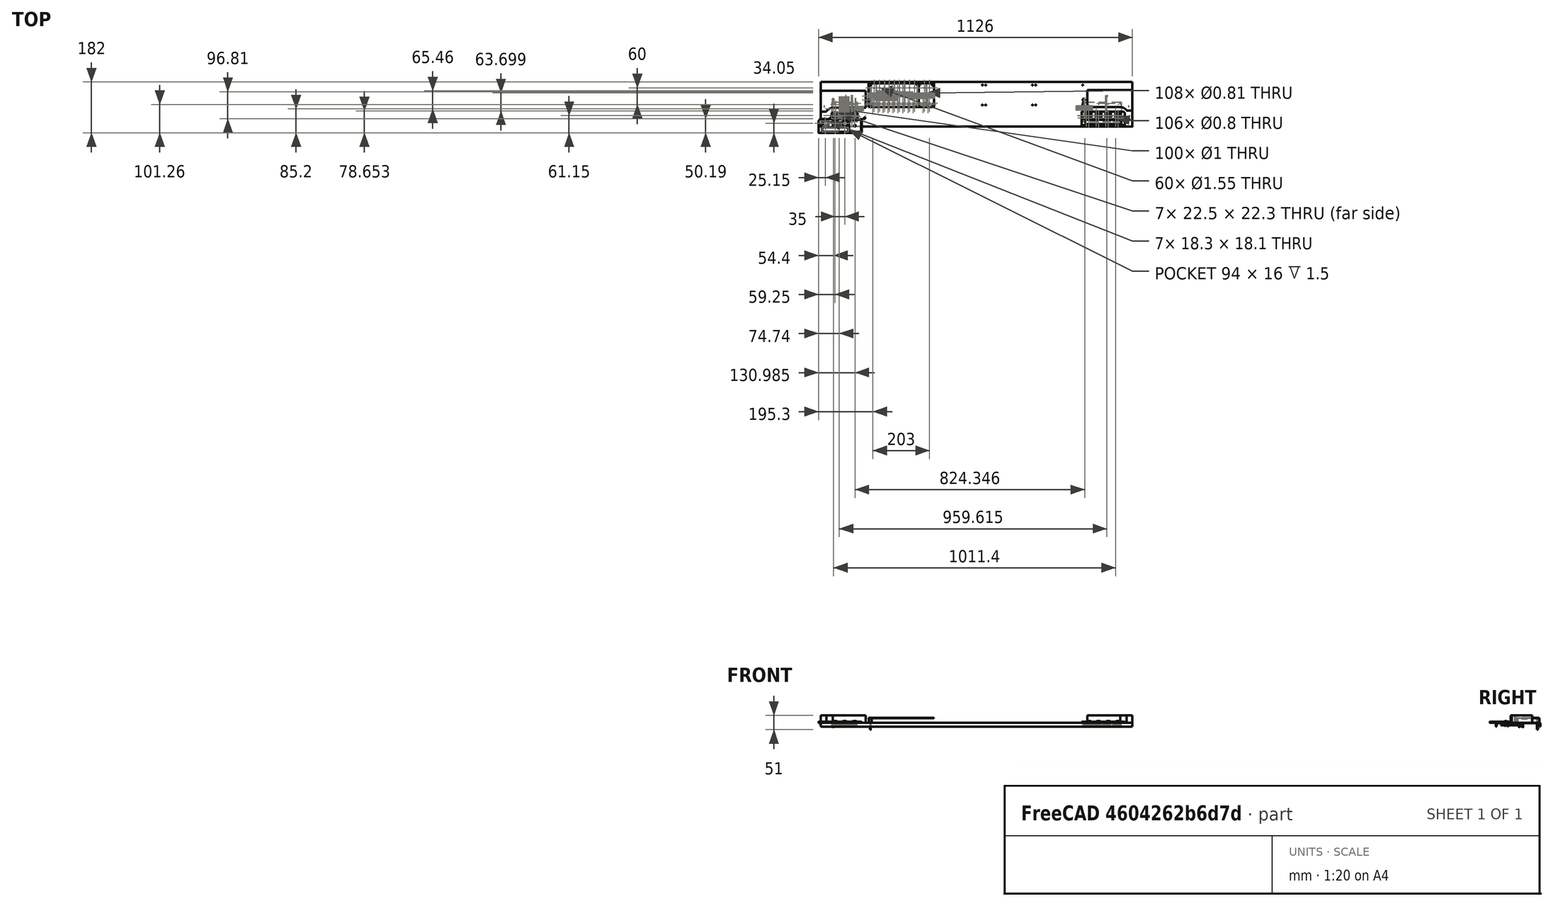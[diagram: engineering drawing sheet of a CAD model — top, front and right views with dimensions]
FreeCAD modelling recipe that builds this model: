
FCSTD DOCUMENT  (FreeCAD 0.20R29603 (Git))
Label: panneau-commandes-assy
License: Public Domain
LicenseURL: http://en.wikipedia.org/wiki/Public_domain
objects: App::FeaturePython×46, Part::FeaturePython×19, PartDesign::CoordinateSystem×2
note: 21 computed .brp shape members not serialized (recipe doc carries the construction recipe); baked Part::Feature solids carry a one-line shape summary decoded from their .brp

FEATURE [Part::FeaturePython] b_PanneauCommandeSupportTirettes_001_  label="PanneauCommandeSupportTirettes_001"  # a2plus imported part (geometry in sourceFile) (typed FeaturePython)
  a2p_Version = 0.4.60k
  fixedPosition = true
  muxInfo = <blob: 10594 chars omitted>
  objectType = a2pPart
  sourceFile = ./../Alu/PanneauCommandeSupportTirettes.FCStd
  subassemblyImport = false
  timeLastImport = 1.68744e+09
  updateColors = true
FEATURE [Part::FeaturePython] b_EnjoliveurBoutonsGaucheAvecFixation_001_  label="EnjoliveurBoutonsGaucheAvecFixation_001"  # a2plus imported part (geometry in sourceFile) (typed FeaturePython)
  Placement = pos=(-8,-25,-1.58671e-06) rot=(0,0,1;0rad)
  a2p_Version = 0.4.60k
  fixedPosition = false
  muxInfo = <blob: 7269 chars omitted>
  objectType = a2pPart
  sourceFile = ./../Accessoires/EnjoliveurBoutonsGaucheAvecFixation.FCStd
  subassemblyImport = false
  timeLastImport = 1.68148e+09
  updateColors = true
FEATURE [Part::FeaturePython] b_BlocLateralPanneauControle_001_  label="BlocLateralPanneauControle_001"  # a2plus imported part (geometry in sourceFile) (typed FeaturePython)
  Placement = pos=(0,51,0) rot=(0,0,1;0rad)
  a2p_Version = 0.4.60k
  fixedPosition = false
  muxInfo = [VERTEXES] | V;Pad;1; | V;Pad;2; | V;Pad;3; | V;Pad;4; | V;Pad;5; | V;Pad;6; | V;Pad;7; | V;Pad;8; | V;Pad;9; | V;Pad;10; | V;Pad;11; | V;Pad;12; | [EDGES] | E;Pad;1; | E;Pad;2; | E;Pad;3; | E;Pad;4; | E;Pad;5; | E;Pad;6; | E;Pad;7; | E;Pad;8; | E;Pad;9; | E;Pad;10; | E;Pad;11; | E;Pad;12; | E;Pad;13; | E;Pad;14; | E;Pad;15; | E;Pad;16; | E;Pad;17; | E;Pad;18; | [FACES] | F;Pad;1; | F;Pad;2; | F;Pad;3; | F;Pad;4; | F;Pad;5; | F;Pad;6; | F;Pad;7; | F;Pad;8;
  objectType = a2pPart
  sourceFile = ./../Menuiserie/BlocLateralPanneauControle.fcstd
  subassemblyImport = false
  timeLastImport = 1.68025e+09
  updateColors = true
FEATURE [Part::FeaturePython] b_BlocLateralPanneauControle_001_001  label="BlocLateralPanneauControle_002"  # a2plus imported part (geometry in sourceFile) (typed FeaturePython)
  Placement = pos=(1118,54.2049,26) rot=(0,1,0;3.14159rad)
  a2p_Version = 0.4.60k
  fixedPosition = false
  muxInfo = [VERTEXES] | V;Pad;1; | V;Pad;2; | V;Pad;3; | V;Pad;4; | V;Pad;5; | V;Pad;6; | V;Pad;7; | V;Pad;8; | V;Pad;9; | V;Pad;10; | V;Pad;11; | V;Pad;12; | [EDGES] | E;Pad;1; | E;Pad;2; | E;Pad;3; | E;Pad;4; | E;Pad;5; | E;Pad;6; | E;Pad;7; | E;Pad;8; | E;Pad;9; | E;Pad;10; | E;Pad;11; | E;Pad;12; | E;Pad;13; | E;Pad;14; | E;Pad;15; | E;Pad;16; | E;Pad;17; | E;Pad;18; | [FACES] | F;Pad;1; | F;Pad;2; | F;Pad;3; | F;Pad;4; | F;Pad;5; | F;Pad;6; | F;Pad;7; | F;Pad;8;
  objectType = a2pPart
  sourceFile = ./../Menuiserie/BlocLateralPanneauControle.fcstd
  subassemblyImport = false
  timeLastImport = 1.68148e+09
  updateColors = true
FEATURE [Part::FeaturePython] b_EnjoliveurBoutonsDroiteAvecFixation_001_  label="EnjoliveurBoutonsDroiteAvecFixation_001"  # a2plus imported part (geometry in sourceFile) (typed FeaturePython)
  Placement = pos=(936.6,2.1,2.92325e-06) rot=(0,0,1;0rad)
  a2p_Version = 0.4.60k
  fixedPosition = false
  muxInfo = <blob: 8591 chars omitted>
  objectType = a2pPart
  sourceFile = ./../Accessoires/EnjoliveurBoutonsDroiteAvecFixation.FCStd
  subassemblyImport = false
  timeLastImport = 1.68148e+09
  updateColors = true
FEATURE [Part::FeaturePython] b_percussions_expr_pedal_001_  label="percussions_expr_pedal_001"  # a2plus imported part (geometry in sourceFile) (typed FeaturePython)
  Placement = pos=(939.7,14.3,-9.58) rot=(0,0,1;0rad)
  a2p_Version = 0.4.60k
  fixedPosition = false
  muxInfo = <blob: 161799 chars omitted>
  objectType = a2pPart
  sourceFile = ./percussions_expr_pedal.FCStd
  subassemblyImport = false
  timeLastImport = 1.68025e+09
  updateColors = true
FEATURE [Part::FeaturePython] b_vibrato_chorus_leslie_001_  label="vibrato_chorus_leslie_001"  # a2plus imported part (geometry in sourceFile) (typed FeaturePython)
  Placement = pos=(41.1,85.2,-9.58) rot=(0,0,1;0rad)
  a2p_Version = 0.4.60k
  fixedPosition = false
  muxInfo = <blob: 126907 chars omitted>
  objectType = a2pPart
  sourceFile = ./vibrato_chorus_leslie.FCStd
  subassemblyImport = false
  timeLastImport = 1.68025e+09
  updateColors = true
FEATURE [App::FeaturePython] axisCoincident_002  label="axisCoincident_002__PanneauCommandeSupportTirettes_001"  # a2plus constraint (typed FeaturePython)
  Object1 = b_percussions_expr_pedal_001_
  Object2 = b_PanneauCommandeSupportTirettes_001_
  ParentTreeObject = -> b_percussions_expr_pedal_001_
  SubElement1 = Edge834
  SubElement2 = Edge197
  Suppressed = false
  Type = axial
  directionConstraint = 0
  lockRotation = false
FEATURE [App::FeaturePython] axisCoincident_002_mirror  label="axisCoincident_002__percussions_expr_pedal_001"  # a2plus constraint (typed FeaturePython)
  Object1 = b_percussions_expr_pedal_001_
  Object2 = b_PanneauCommandeSupportTirettes_001_
  ParentTreeObject = -> b_PanneauCommandeSupportTirettes_001_
  SubElement1 = Edge834
  SubElement2 = Edge197
  Suppressed = false
  Type = axial
  directionConstraint = 0
  lockRotation = false
FEATURE [App::FeaturePython] planeCoincident_002  label="planeCoincident_002__percussions_expr_pedal_001"  # a2plus constraint (typed FeaturePython)
  Object1 = b_PanneauCommandeSupportTirettes_001_
  Object2 = b_percussions_expr_pedal_001_
  ParentTreeObject = -> b_PanneauCommandeSupportTirettes_001_
  SubElement1 = Face12
  SubElement2 = Face265
  Suppressed = false
  Type = plane
  directionConstraint = 1
  offset = 6
FEATURE [App::FeaturePython] planeCoincident_002_mirror  label="planeCoincident_002__PanneauCommandeSupportTirettes_001"  # a2plus constraint (typed FeaturePython)
  Object1 = b_PanneauCommandeSupportTirettes_001_
  Object2 = b_percussions_expr_pedal_001_
  ParentTreeObject = -> b_percussions_expr_pedal_001_
  SubElement1 = Face12
  SubElement2 = Face265
  Suppressed = false
  Type = plane
  directionConstraint = 1
  offset = 6
FEATURE [Part::FeaturePython] b_entretoise_cartes_vc_perc_001_  label="entretoise-cartes-vc-perc_001"  # a2plus imported part (geometry in sourceFile) (typed FeaturePython)
  Placement = pos=(44.8,81.5,-8) rot=(0,0,1;0rad)
  a2p_Version = 0.4.60k
  fixedPosition = false
  muxInfo = [VERTEXES] | V;Pad;1;4; | V;Pad;2;4; | V;Pad;3;4; | V;Pad;4;4; | [EDGES] | E;Pad;1;6; | E;Pad;2;6; | E;Pad;3;6; | E;Pad;4;6; | E;Pad;5;6; | E;Pad;6;6; | [FACES] | F;Pad;1;4; | F;Pad;2;4; | F;Pad;3;4; | F;Pad;4;4;
  objectType = a2pPart
  sourceFile = ./../Accessoires/entretoise-cartes-vc-perc.FCStd
  subassemblyImport = false
  timeLastImport = 1.68025e+09
  updateColors = true
FEATURE [App::FeaturePython] planeCoincident_003  label="planeCoincident_003__PanneauCommandeSupportTirettes_001"  # a2plus constraint (typed FeaturePython)
  Object1 = b_entretoise_cartes_vc_perc_001_
  Object2 = b_PanneauCommandeSupportTirettes_001_
  ParentTreeObject = -> b_entretoise_cartes_vc_perc_001_
  SubElement1 = Face4
  SubElement2 = Face12
  Suppressed = false
  Type = plane
  directionConstraint = 0
  offset = 0
FEATURE [App::FeaturePython] planeCoincident_003_mirror  label="planeCoincident_003__entretoise-cartes-vc-perc_001"  # a2plus constraint (typed FeaturePython)
  Object1 = b_entretoise_cartes_vc_perc_001_
  Object2 = b_PanneauCommandeSupportTirettes_001_
  ParentTreeObject = -> b_PanneauCommandeSupportTirettes_001_
  SubElement1 = Face4
  SubElement2 = Face12
  Suppressed = false
  Type = plane
  directionConstraint = 0
  offset = 0
FEATURE [App::FeaturePython] axisCoincident_003  label="axisCoincident_003__PanneauCommandeSupportTirettes_001"  # a2plus constraint (typed FeaturePython)
  Object1 = b_entretoise_cartes_vc_perc_001_
  Object2 = b_PanneauCommandeSupportTirettes_001_
  ParentTreeObject = -> b_entretoise_cartes_vc_perc_001_
  SubElement1 = Edge3
  SubElement2 = Edge77
  Suppressed = false
  Type = axial
  directionConstraint = 0
  lockRotation = false
FEATURE [App::FeaturePython] axisCoincident_003_mirror  label="axisCoincident_003__entretoise-cartes-vc-perc_001"  # a2plus constraint (typed FeaturePython)
  Object1 = b_entretoise_cartes_vc_perc_001_
  Object2 = b_PanneauCommandeSupportTirettes_001_
  ParentTreeObject = -> b_PanneauCommandeSupportTirettes_001_
  SubElement1 = Edge3
  SubElement2 = Edge77
  Suppressed = false
  Type = axial
  directionConstraint = 0
  lockRotation = false
FEATURE [Part::FeaturePython] Screw  label="M3x16-Screw"  # Fasteners workbench fastener (typed FeaturePython)
  Placement = pos=(44.8,81.5,0) rot=(0,0,1;0rad)
  diameter = 4
  invert = false
  leftHanded = false
  length = 6
  lengthCustom = 16
  matchOuter = false
  offset = 0
  thread = true
  type = 47
FEATURE [App::FeaturePython] planeCoincident_004  label="planeCoincident_004__PanneauCommandeSupportTirettes_001"  # a2plus constraint (typed FeaturePython)
  Object1 = b_vibrato_chorus_leslie_001_
  Object2 = b_PanneauCommandeSupportTirettes_001_
  ParentTreeObject = -> b_vibrato_chorus_leslie_001_
  SubElement1 = Face785
  SubElement2 = Face12
  Suppressed = false
  Type = plane
  directionConstraint = 1
  offset = 6
FEATURE [App::FeaturePython] planeCoincident_004_mirror  label="planeCoincident_004__vibrato_chorus_leslie_001"  # a2plus constraint (typed FeaturePython)
  Object1 = b_vibrato_chorus_leslie_001_
  Object2 = b_PanneauCommandeSupportTirettes_001_
  ParentTreeObject = -> b_PanneauCommandeSupportTirettes_001_
  SubElement1 = Face785
  SubElement2 = Face12
  Suppressed = false
  Type = plane
  directionConstraint = 1
  offset = 6
FEATURE [App::FeaturePython] planeCoincident_005_mirror  label="planeCoincident_005__M6-Washer"  # a2plus constraint (typed FeaturePython)
  Object1 = Washer
  Object2 = b_vibrato_chorus_leslie_001_
  ParentTreeObject = -> b_vibrato_chorus_leslie_001_
  SubElement1 = Face1
  SubElement2 = Face784
  Suppressed = false
  Type = plane
  directionConstraint = 1
  offset = 0
FEATURE [App::FeaturePython] axisCoincident_004_mirror  label="axisCoincident_004__M4-Washer"  # a2plus constraint (typed FeaturePython)
  Object1 = Washer
  Object2 = b_vibrato_chorus_leslie_001_
  ParentTreeObject = -> b_vibrato_chorus_leslie_001_
  SubElement1 = Edge5
  SubElement2 = Edge2334
  Suppressed = false
  Type = axial
  directionConstraint = 0
  lockRotation = false
FEATURE [Part::FeaturePython] Washer  label="#5-Washer"  # Fasteners workbench fastener (typed FeaturePython)
  Placement = pos=(44.8,81.5,-10.3928) rot=(0,0,1;0rad)
  diameter = 6
  invert = false
  matchOuter = false
  offset = 0
  type = 0
FEATURE [App::FeaturePython] planeCoincident_005  label="planeCoincident_005__vibrato_chorus_leslie_001"  # a2plus constraint (typed FeaturePython)
  Object1 = Washer
  Object2 = b_vibrato_chorus_leslie_001_
  ParentTreeObject = -> Washer
  SubElement1 = Face1
  SubElement2 = Face784
  Suppressed = false
  Type = plane
  directionConstraint = 1
  offset = 0
FEATURE [App::FeaturePython] axisCoincident_004  label="axisCoincident_004__vibrato_chorus_leslie_001"  # a2plus constraint (typed FeaturePython)
  Object1 = Washer
  Object2 = b_vibrato_chorus_leslie_001_
  ParentTreeObject = -> Washer
  SubElement1 = Edge5
  SubElement2 = Edge2334
  Suppressed = false
  Type = axial
  directionConstraint = 0
  lockRotation = false
FEATURE [App::FeaturePython] planeCoincident_006  label="planeCoincident_006__vibrato_chorus_leslie_001"  # a2plus constraint (typed FeaturePython)
  Object1 = Washer
  Object2 = b_vibrato_chorus_leslie_001_
  ParentTreeObject = -> Washer
  SubElement1 = Face1
  SubElement2 = Face784
  Suppressed = false
  Type = plane
  directionConstraint = 1
  offset = 0
FEATURE [App::FeaturePython] planeCoincident_006_mirror  label="planeCoincident_006__#5-Washer"  # a2plus constraint (typed FeaturePython)
  Object1 = Washer
  Object2 = b_vibrato_chorus_leslie_001_
  ParentTreeObject = -> b_vibrato_chorus_leslie_001_
  SubElement1 = Face1
  SubElement2 = Face784
  Suppressed = false
  Type = plane
  directionConstraint = 1
  offset = 0
FEATURE [Part::FeaturePython] Nut  label="M3-Nut"  # Fasteners workbench fastener (typed FeaturePython)
  Placement = pos=(44.8,81.5,-12.7928) rot=(0,0,1;0rad)
  diameter = 4
  invert = false
  leftHanded = false
  matchOuter = false
  offset = 0
  thread = false
  type = 22
FEATURE [App::FeaturePython] planeCoincident_007  label="planeCoincident_007__#5-Washer"  # a2plus constraint (typed FeaturePython)
  Object1 = Nut
  Object2 = Washer
  ParentTreeObject = -> Nut
  SubElement1 = Face3
  SubElement2 = Face3
  Suppressed = false
  Type = plane
  directionConstraint = 0
  offset = 0
FEATURE [App::FeaturePython] planeCoincident_007_mirror  label="planeCoincident_007__M6-Nut"  # a2plus constraint (typed FeaturePython)
  Object1 = Nut
  Object2 = Washer
  ParentTreeObject = -> Washer
  SubElement1 = Face3
  SubElement2 = Face3
  Suppressed = false
  Type = plane
  directionConstraint = 0
  offset = 0
FEATURE [App::FeaturePython] axisCoincident_005  label="axisCoincident_005__#5-Washer"  # a2plus constraint (typed FeaturePython)
  Object1 = Nut
  Object2 = Washer
  ParentTreeObject = -> Nut
  SubElement1 = Edge4
  SubElement2 = Edge3
  Suppressed = false
  Type = axial
  directionConstraint = 0
  lockRotation = false
FEATURE [App::FeaturePython] axisCoincident_005_mirror  label="axisCoincident_005__M6-Nut"  # a2plus constraint (typed FeaturePython)
  Object1 = Nut
  Object2 = Washer
  ParentTreeObject = -> Washer
  SubElement1 = Edge4
  SubElement2 = Edge3
  Suppressed = false
  Type = axial
  directionConstraint = 0
  lockRotation = false
FEATURE [App::FeaturePython] planeCoincident_008  label="planeCoincident_008__#5-Washer"  # a2plus constraint (typed FeaturePython)
  Object1 = Nut
  Object2 = Washer
  ParentTreeObject = -> Nut
  SubElement1 = Face3
  SubElement2 = Face3
  Suppressed = false
  Type = plane
  directionConstraint = 0
  offset = 0
FEATURE [App::FeaturePython] planeCoincident_008_mirror  label="planeCoincident_008__M3-Nut"  # a2plus constraint (typed FeaturePython)
  Object1 = Nut
  Object2 = Washer
  ParentTreeObject = -> Washer
  SubElement1 = Face3
  SubElement2 = Face3
  Suppressed = false
  Type = plane
  directionConstraint = 0
  offset = 0
FEATURE [Part::FeaturePython] Screw001  label="M2x6-Screw"  # Fasteners workbench fastener (typed FeaturePython)
  Placement = pos=(-1.35631e-08,-8.06109e-09,0.999998) rot=(0,0,1;0rad)
  diameter = 2
  invert = false
  leftHanded = false
  length = 10
  lengthCustom = 6
  matchOuter = false
  offset = 0
  thread = true
  type = 46
FEATURE [App::FeaturePython] planeCoincident_011  label="planeCoincident_011__M6-Washer"  # a2plus constraint (typed FeaturePython)
  Object1 = Screw002
  Object2 = Washer001
  SubElement1 = Face11
  SubElement2 = Face1
  Suppressed = false
  Type = plane
  directionConstraint = 0
  offset = 0
FEATURE [App::FeaturePython] planeCoincident_011_mirror  label="planeCoincident_011__M6x12-Screw"  # a2plus constraint (typed FeaturePython)
  Object1 = Screw002
  Object2 = Washer001
  SubElement1 = Face11
  SubElement2 = Face1
  Suppressed = false
  Type = plane
  directionConstraint = 0
  offset = 0
FEATURE [App::FeaturePython] planeCoincident_012  label="planeCoincident_012__PanneauCommandeSupportTirettes_001"  # a2plus constraint (typed FeaturePython)
  Object1 = Washer001
  Object2 = b_PanneauCommandeSupportTirettes_001_
  SubElement1 = Face3
  SubElement2 = Face11
  Suppressed = false
  Type = plane
  directionConstraint = 0
  offset = 0
FEATURE [App::FeaturePython] planeCoincident_012_mirror  label="planeCoincident_012__M6-Washer"  # a2plus constraint (typed FeaturePython)
  Object1 = Washer001
  Object2 = b_PanneauCommandeSupportTirettes_001_
  SubElement1 = Face3
  SubElement2 = Face11
  Suppressed = false
  Type = plane
  directionConstraint = 0
  offset = 0
FEATURE [App::FeaturePython] axisCoincident_008  label="axisCoincident_008__PanneauCommandeSupportTirettes_001"  # a2plus constraint (typed FeaturePython)
  Object1 = Washer001
  Object2 = b_PanneauCommandeSupportTirettes_001_
  SubElement1 = Edge1
  SubElement2 = Edge27
  Suppressed = false
  Type = axial
  directionConstraint = 0
  lockRotation = false
FEATURE [App::FeaturePython] axisCoincident_008_mirror  label="axisCoincident_008__M6-Washer"  # a2plus constraint (typed FeaturePython)
  Object1 = Washer001
  Object2 = b_PanneauCommandeSupportTirettes_001_
  SubElement1 = Edge1
  SubElement2 = Edge27
  Suppressed = false
  Type = axial
  directionConstraint = 0
  lockRotation = false
FEATURE [App::FeaturePython] axisCoincident_009  label="axisCoincident_009__M6-Washer"  # a2plus constraint (typed FeaturePython)
  Object1 = Screw002
  Object2 = Washer001
  SubElement1 = Edge5
  SubElement2 = Edge2
  Suppressed = false
  Type = axial
  directionConstraint = 0
  lockRotation = false
FEATURE [App::FeaturePython] axisCoincident_009_mirror  label="axisCoincident_009__M6x12-Screw"  # a2plus constraint (typed FeaturePython)
  Object1 = Screw002
  Object2 = Washer001
  SubElement1 = Edge5
  SubElement2 = Edge2
  Suppressed = false
  Type = axial
  directionConstraint = 0
  lockRotation = false
FEATURE [Part::FeaturePython] Screw003  label="M4x16-Screw"  # Fasteners workbench fastener (typed FeaturePython)
  Placement = pos=(44.8,93.1,-3.13578e-07) rot=(0,0,1;0rad)
  baseObject = -> b_PanneauCommandeSupportTirettes_001_ [Edge218]
  diameter = 6
  invert = false
  leftHanded = false
  length = 11
  lengthCustom = 16
  matchOuter = false
  offset = 0
  thread = true
  type = 47
FEATURE [App::FeaturePython] axisCoincident_007  label="axisCoincident_007__PanneauCommandeSupportTirettes_001"  # a2plus constraint (typed FeaturePython)
  Object1 = Screw003
  Object2 = b_PanneauCommandeSupportTirettes_001_
  ParentTreeObject = -> Screw003
  SubElement1 = Edge165
  SubElement2 = Edge79
  Suppressed = false
  Type = axial
  directionConstraint = 0
  lockRotation = false
FEATURE [App::FeaturePython] axisCoincident_007_mirror  label="axisCoincident_007__M4x16-Screw"  # a2plus constraint (typed FeaturePython)
  Object1 = Screw003
  Object2 = b_PanneauCommandeSupportTirettes_001_
  ParentTreeObject = -> b_PanneauCommandeSupportTirettes_001_
  SubElement1 = Edge165
  SubElement2 = Edge79
  Suppressed = false
  Type = axial
  directionConstraint = 0
  lockRotation = false
FEATURE [App::FeaturePython] planeCoincident_001  label="planeCoincident_001__PanneauCommandeSupportTirettes_001"  # a2plus constraint (typed FeaturePython)
  Object1 = Screw003
  Object2 = b_PanneauCommandeSupportTirettes_001_
  ParentTreeObject = -> Screw003
  SubElement1 = Face83
  SubElement2 = Face11
  Suppressed = false
  Type = plane
  directionConstraint = 0
  offset = 0
FEATURE [App::FeaturePython] planeCoincident_001_mirror  label="planeCoincident_001__M4x16-Screw"  # a2plus constraint (typed FeaturePython)
  Object1 = Screw003
  Object2 = b_PanneauCommandeSupportTirettes_001_
  ParentTreeObject = -> b_PanneauCommandeSupportTirettes_001_
  SubElement1 = Face83
  SubElement2 = Face11
  Suppressed = false
  Type = plane
  directionConstraint = 0
  offset = 0
FEATURE [App::FeaturePython] planeCoincident_009  label="planeCoincident_009__PanneauCommandeSupportTirettes_001"  # a2plus constraint (typed FeaturePython)
  Object1 = b_BlocLateralPanneauControle_001_001
  Object2 = b_PanneauCommandeSupportTirettes_001_
  ParentTreeObject = -> b_BlocLateralPanneauControle_001_001
  SubElement1 = Face8
  SubElement2 = Face11
  Suppressed = false
  Type = plane
  directionConstraint = 0
  offset = 0
FEATURE [App::FeaturePython] planeCoincident_009_mirror  label="planeCoincident_009__BlocLateralPanneauControle_002"  # a2plus constraint (typed FeaturePython)
  Object1 = b_BlocLateralPanneauControle_001_001
  Object2 = b_PanneauCommandeSupportTirettes_001_
  ParentTreeObject = -> b_PanneauCommandeSupportTirettes_001_
  SubElement1 = Face8
  SubElement2 = Face11
  Suppressed = false
  Type = plane
  directionConstraint = 0
  offset = 0
FEATURE [App::FeaturePython] planeCoincident_010  label="planeCoincident_010__PanneauCommandeSupportTirettes_001"  # a2plus constraint (typed FeaturePython)
  Object1 = b_BlocLateralPanneauControle_001_001
  Object2 = b_PanneauCommandeSupportTirettes_001_
  ParentTreeObject = -> b_BlocLateralPanneauControle_001_001
  SubElement1 = Face3
  SubElement2 = Face1
  Suppressed = false
  Type = plane
  directionConstraint = 0
  offset = 0
FEATURE [App::FeaturePython] planeCoincident_010_mirror  label="planeCoincident_010__BlocLateralPanneauControle_002"  # a2plus constraint (typed FeaturePython)
  Object1 = b_BlocLateralPanneauControle_001_001
  Object2 = b_PanneauCommandeSupportTirettes_001_
  ParentTreeObject = -> b_PanneauCommandeSupportTirettes_001_
  SubElement1 = Face3
  SubElement2 = Face1
  Suppressed = false
  Type = plane
  directionConstraint = 0
  offset = 0
FEATURE [Part::FeaturePython] b_entretoise_simple_carte_tirettes_001_  label="entretoise-simple-carte-tirettes_001"  # a2plus imported part (geometry in sourceFile) (typed FeaturePython)
  Placement = pos=(177.9,152.65,-4.91077e-07) rot=(0,0,-1;1.5708rad)
  a2p_Version = 0.4.60k
  fixedPosition = false
  muxInfo = <blob: 2578 chars omitted>
  objectType = a2pPart
  sourceFile = ./../Accessoires/Entretoise-Carte-Tirettes/entretoise-simple-carte-tirettes.FCStd
  subassemblyImport = false
  timeLastImport = 1.68036e+09
  updateColors = true
FEATURE [App::FeaturePython] axisCoincident_010  label="axisCoincident_010__entretoise-simple-carte-tirettes_001"  # a2plus constraint (typed FeaturePython)
  Object1 = b_PanneauCommandeSupportTirettes_001_
  Object2 = b_entretoise_simple_carte_tirettes_001_
  ParentTreeObject = -> b_PanneauCommandeSupportTirettes_001_
  SubElement1 = Edge81
  SubElement2 = Edge63
  Suppressed = false
  Type = axial
  directionConstraint = 0
  lockRotation = false
FEATURE [App::FeaturePython] axisCoincident_010_mirror  label="axisCoincident_010__PanneauCommandeSupportTirettes_001"  # a2plus constraint (typed FeaturePython)
  Object1 = b_PanneauCommandeSupportTirettes_001_
  Object2 = b_entretoise_simple_carte_tirettes_001_
  ParentTreeObject = -> b_entretoise_simple_carte_tirettes_001_
  SubElement1 = Edge81
  SubElement2 = Edge63
  Suppressed = false
  Type = axial
  directionConstraint = 0
  lockRotation = false
FEATURE [PartDesign::CoordinateSystem] a2pLCS
  AttacherType = Attacher::AttachEngine3D
FEATURE [Part::FeaturePython] b_LCS_Collection_  label="LCS_Collection"  # WARN: FeaturePython — macro-defined, semantics opaque (R4)
  Group = -> [a2pLCS]
  Owner = b_drawbars_pcb_small_001_
  Placement = pos=(118.644,-142.112,-14.8964) rot=(0,0,1;0rad)
FEATURE [Part::FeaturePython] b_drawbars_pcb_small_001_  label="drawbars_pcb_small_001"  # a2plus imported part (geometry in sourceFile) (typed FeaturePython)
  Placement = pos=(172.1,151.9,17.6) rot=(0,0,1;0rad)
  a2p_Version = 0.4.60k
  fixedPosition = false
  lcsLink = -> [b_LCS_Collection_]
  muxInfo = <blob: 35043 chars omitted>
  objectType = a2pPart
  sourceFile = ./drawbars_pcb_small.FCStd
  subassemblyImport = false
  timeLastImport = 1.68036e+09
  updateColors = true
FEATURE [Part::FeaturePython] Screw004  label="(M3.5)x25-Screw"  # Fasteners workbench fastener (typed FeaturePython)
  Placement = pos=(177.9,146,0) rot=(0,0,1;0rad)
  baseObject = -> b_PanneauCommandeSupportTirettes_001_ [Edge78]
  diameter = 5
  invert = false
  leftHanded = false
  length = 11
  lengthCustom = 25
  matchOuter = false
  offset = 0
  thread = false
  type = 46
FEATURE [Part::FeaturePython] Nut001  label="M3-Nut001"  # Fasteners workbench fastener (typed FeaturePython)
  Placement = pos=(0,0,-4.4) rot=(0,0,1;0rad)
  diameter = 4
  invert = false
  leftHanded = false
  matchOuter = false
  offset = 0
  thread = false
  type = 22
FEATURE [PartDesign::CoordinateSystem] a2pLCS001
  AttacherType = Attacher::AttachEngine3D
FEATURE [Part::FeaturePython] b_LCS_Collection_001  label="LCS_Collection001"  # WARN: FeaturePython — macro-defined, semantics opaque (R4)
  Group = -> [a2pLCS001]
  Owner = CachedObject_8
FEATURE [App::FeaturePython] axisCoincident_011  label="axisCoincident_011__EnjoliveurBoutonsGaucheAvecFixation_001"  # a2plus constraint (typed FeaturePython)
  Object1 = Nut001
  Object2 = b_EnjoliveurBoutonsGaucheAvecFixation_001_
  ParentTreeObject = -> Nut001
  SubElement1 = Edge2
  SubElement2 = Edge82
  Suppressed = false
  Type = axial
  directionConstraint = 0
  lockRotation = false
FEATURE [App::FeaturePython] axisCoincident_011_mirror  label="axisCoincident_011__M3-Nut001"  # a2plus constraint (typed FeaturePython)
  Object1 = Nut001
  Object2 = b_EnjoliveurBoutonsGaucheAvecFixation_001_
  ParentTreeObject = -> b_EnjoliveurBoutonsGaucheAvecFixation_001_
  SubElement1 = Edge2
  SubElement2 = Edge82
  Suppressed = false
  Type = axial
  directionConstraint = 0
  lockRotation = false
FEATURE [App::FeaturePython] planeCoincident_013  label="planeCoincident_013__PanneauCommandeSupportTirettes_001"  # a2plus constraint (typed FeaturePython)
  Object1 = Nut001
  Object2 = b_PanneauCommandeSupportTirettes_001_
  ParentTreeObject = -> Nut001
  SubElement1 = Face3
  SubElement2 = Face12
  Suppressed = false
  Type = plane
  directionConstraint = 0
  offset = 0
FEATURE [App::FeaturePython] planeCoincident_013_mirror  label="planeCoincident_013__M3-Nut001"  # a2plus constraint (typed FeaturePython)
  Object1 = Nut001
  Object2 = b_PanneauCommandeSupportTirettes_001_
  ParentTreeObject = -> b_PanneauCommandeSupportTirettes_001_
  SubElement1 = Face3
  SubElement2 = Face12
  Suppressed = false
  Type = plane
  directionConstraint = 0
  offset = 0
FEATURE [App::FeaturePython] axisCoincident_012  label="axisCoincident_012__M2x6-Screw"  # a2plus constraint (typed FeaturePython)
  Object1 = Nut001
  Object2 = Screw001
  ParentTreeObject = -> Nut001
  SubElement1 = Edge2
  SubElement2 = Edge22
  Suppressed = false
  Type = axial
  directionConstraint = 0
  lockRotation = false
FEATURE [App::FeaturePython] axisCoincident_012_mirror  label="axisCoincident_012__M3-Nut001"  # a2plus constraint (typed FeaturePython)
  Object1 = Nut001
  Object2 = Screw001
  ParentTreeObject = -> Screw001
  SubElement1 = Edge2
  SubElement2 = Edge22
  Suppressed = false
  Type = axial
  directionConstraint = 0
  lockRotation = false
